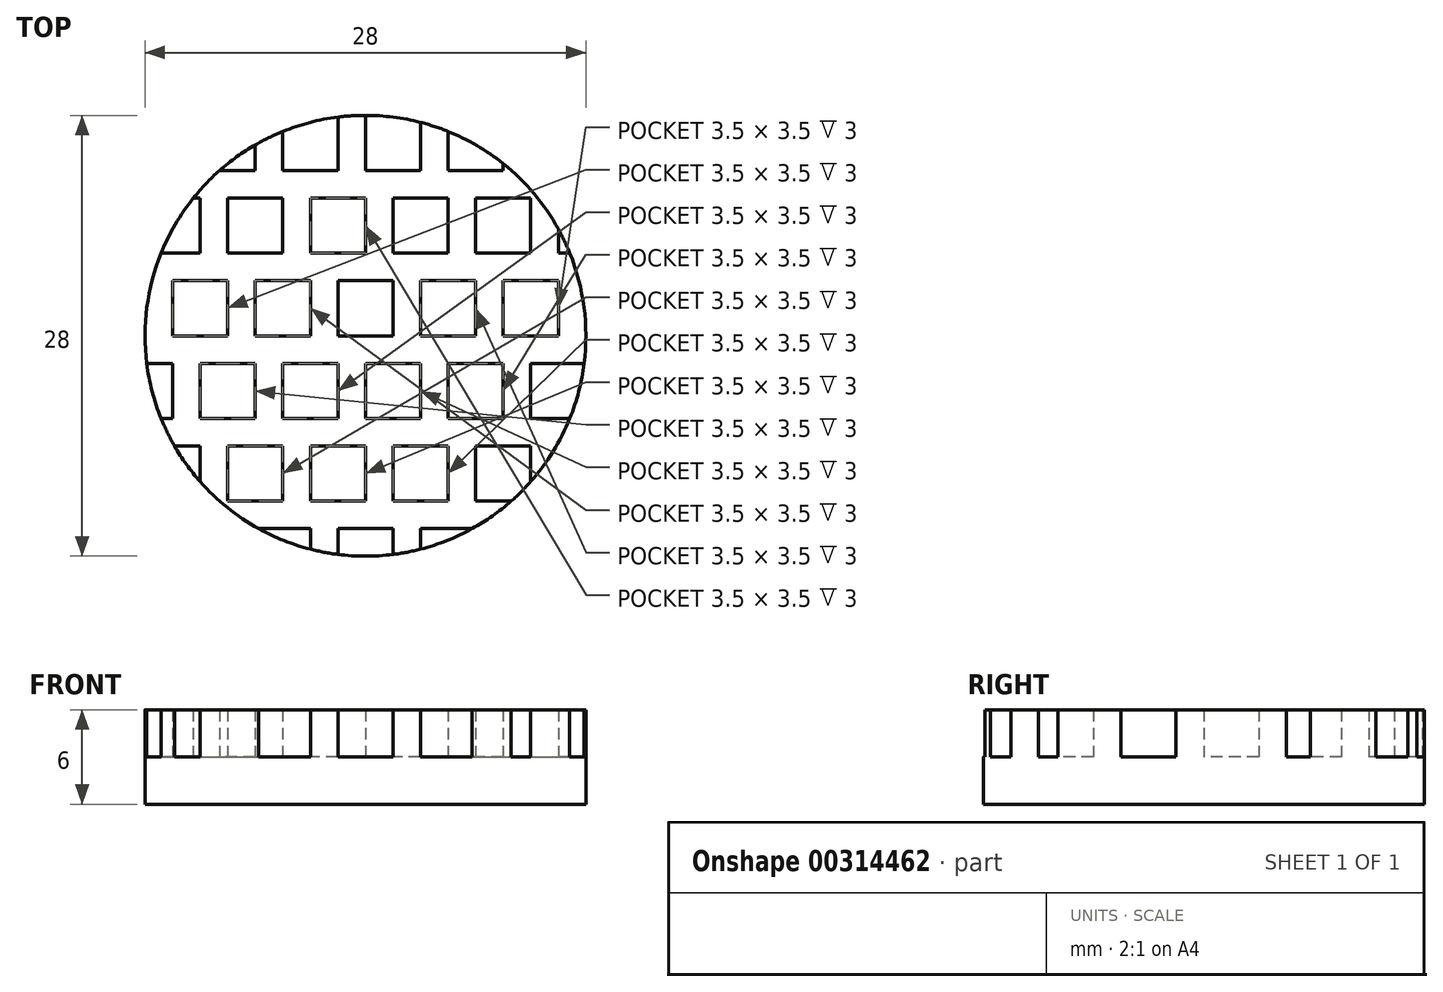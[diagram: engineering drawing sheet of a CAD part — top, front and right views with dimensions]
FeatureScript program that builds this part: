
annotation { "Feature Type Name" : "Feature", "Feature Type Description" : "" }
export const myFeature = defineFeature(function(context is Context, id is Id, definition is map)
    precondition{}
    {
        {
            var Q0;
            Q0=qCreatedBy(makeId("Top.planeOp"),FACE);
            var sketch = newSketch(context, id + "F0", { "sketchPlane" : qUnion([Q0])});
            skCircle(sketch, "E0", {"center": v(0, 0) * mm, "radius": 14 * mm});
            skSolve(sketch);
        }
        {
            var Q0;
            Q0=makeQuery(id+"F0.imprint","IMPRINT",FACE,{"disambiguationData":[TD([[makeQuery(id+"F0.imprint","IMPRINT",EDGE,{"derivedFrom":sQuery(id+"F0.wireOp",EDGE,"E0")}),1.0]])]});
            extrude(context, id + "F1", {"entities" : qUnion([Q0]), "depth" : 3 * mm});
        }
        {
            var Q0;
            Q0=makeQuery(id+"F1.opExtrude","CAP_FACE",FACE,{"disambiguationData":[OSD([sQuery(id+"F0.wireOp",EDGE,"E0")])],"isStart":false});
            var sketch = newSketch(context, id + "F2", { "sketchPlane" : qUnion([Q0])});
            skLineSegment(sketch, "E1.bottom", {"start": v(-10.5, 14) * mm, "end": v(-7, 14) * mm});
            skLineSegment(sketch, "E1.top", {"start": v(-10.5, 10.5) * mm, "end": v(-7, 10.5) * mm});
            skLineSegment(sketch, "E1.left", {"start": v(-10.5, 14) * mm, "end": v(-10.5, 10.5) * mm});
            skLineSegment(sketch, "E1.right", {"start": v(-7, 14) * mm, "end": v(-7, 10.5) * mm});
            skLineSegment(sketch, "E2.1.0.0", {"start": v(-5.25, 10.5) * mm, "end": v(-1.75, 10.5) * mm});
            skLineSegment(sketch, "E2.1.0.1", {"start": v(-5.25, 14) * mm, "end": v(-5.25, 10.5) * mm});
            skLineSegment(sketch, "E2.1.0.2", {"start": v(-1.75, 14) * mm, "end": v(-1.75, 10.5) * mm});
            skLineSegment(sketch, "E2.1.0.3", {"start": v(-5.25, 14) * mm, "end": v(-1.75, 14) * mm});
            skLineSegment(sketch, "E2.2.0.0", {"start": v(0, 10.5) * mm, "end": v(3.5, 10.5) * mm});
            skLineSegment(sketch, "E2.2.0.1", {"start": v(0, 14) * mm, "end": v(0, 10.5) * mm});
            skLineSegment(sketch, "E2.2.0.2", {"start": v(3.5, 14) * mm, "end": v(3.5, 10.5) * mm});
            skLineSegment(sketch, "E2.2.0.3", {"start": v(0, 14) * mm, "end": v(3.5, 14) * mm});
            skLineSegment(sketch, "E2.direction1", {"start": v(-10.5, 10.5) * mm, "end": v(-5.25, 10.5) * mm, "construction": true});
            skLineSegment(sketch, "E3.0.3.0", {"start": v(5.25, 10.5) * mm, "end": v(8.75, 10.5) * mm});
            skLineSegment(sketch, "E3.3.3.0", {"start": v(5.25, 14) * mm, "end": v(5.25, 10.5) * mm});
            skLineSegment(sketch, "E3.6.3.0", {"start": v(8.75, 14) * mm, "end": v(8.75, 10.5) * mm});
            skLineSegment(sketch, "E3.9.3.0", {"start": v(5.25, 14) * mm, "end": v(8.75, 14) * mm});
            skLineSegment(sketch, "E4.0.4.0", {"start": v(10.5, 10.5) * mm, "end": v(14, 10.5) * mm});
            skLineSegment(sketch, "E4.3.4.0", {"start": v(10.5, 14) * mm, "end": v(10.5, 10.5) * mm});
            skLineSegment(sketch, "E4.6.4.0", {"start": v(14, 14) * mm, "end": v(14, 10.5) * mm});
            skLineSegment(sketch, "E4.9.4.0", {"start": v(10.5, 14) * mm, "end": v(14, 14) * mm});
            skLineSegment(sketch, "E5.0.5.0", {"start": v(15.75, 10.5) * mm, "end": v(19.25, 10.5) * mm});
            skLineSegment(sketch, "E5.3.5.0", {"start": v(15.75, 14) * mm, "end": v(15.75, 10.5) * mm});
            skLineSegment(sketch, "E5.6.5.0", {"start": v(19.25, 14) * mm, "end": v(19.25, 10.5) * mm});
            skLineSegment(sketch, "E5.9.5.0", {"start": v(15.75, 14) * mm, "end": v(19.25, 14) * mm});
            skLineSegment(sketch, "E6.0.6.0", {"start": v(21, 10.5) * mm, "end": v(24.5, 10.5) * mm});
            skLineSegment(sketch, "E6.3.6.0", {"start": v(21, 14) * mm, "end": v(21, 10.5) * mm});
            skLineSegment(sketch, "E6.6.6.0", {"start": v(24.5, 14) * mm, "end": v(24.5, 10.5) * mm});
            skLineSegment(sketch, "E6.9.6.0", {"start": v(21, 14) * mm, "end": v(24.5, 14) * mm});
            skLineSegment(sketch, "E6.0.7.0", {"start": v(26.25, 10.5) * mm, "end": v(29.75, 10.5) * mm});
            skLineSegment(sketch, "E6.3.7.0", {"start": v(26.25, 14) * mm, "end": v(26.25, 10.5) * mm});
            skLineSegment(sketch, "E6.6.7.0", {"start": v(29.75, 14) * mm, "end": v(29.75, 10.5) * mm});
            skLineSegment(sketch, "E6.9.7.0", {"start": v(26.25, 14) * mm, "end": v(29.75, 14) * mm});
            skLineSegment(sketch, "E7.0.8.0", {"start": v(31.5, 10.5) * mm, "end": v(35, 10.5) * mm});
            skLineSegment(sketch, "E7.3.8.0", {"start": v(31.5, 14) * mm, "end": v(31.5, 10.5) * mm});
            skLineSegment(sketch, "E7.6.8.0", {"start": v(35, 14) * mm, "end": v(35, 10.5) * mm});
            skLineSegment(sketch, "E7.9.8.0", {"start": v(31.5, 14) * mm, "end": v(35, 14) * mm});
            skLineSegment(sketch, "E8.0.9.0", {"start": v(36.75, 10.5) * mm, "end": v(40.25, 10.5) * mm});
            skLineSegment(sketch, "E8.3.9.0", {"start": v(36.75, 14) * mm, "end": v(36.75, 10.5) * mm});
            skLineSegment(sketch, "E8.6.9.0", {"start": v(40.25, 14) * mm, "end": v(40.25, 10.5) * mm});
            skLineSegment(sketch, "E8.9.9.0", {"start": v(36.75, 14) * mm, "end": v(40.25, 14) * mm});
            skLineSegment(sketch, "E9.1.0.0", {"start": v(10.5, 8.75) * mm, "end": v(10.5, 5.25) * mm});
            skLineSegment(sketch, "E9.1.0.1", {"start": v(21, 8.75) * mm, "end": v(21, 5.25) * mm});
            skLineSegment(sketch, "E9.1.0.2", {"start": v(28, 8.75) * mm, "end": v(31.5, 8.75) * mm});
            skLineSegment(sketch, "E9.1.0.3", {"start": v(7, 8.75) * mm, "end": v(10.5, 8.75) * mm});
            skLineSegment(sketch, "E9.1.0.4", {"start": v(1.75, 8.75) * mm, "end": v(5.25, 8.75) * mm});
            skLineSegment(sketch, "E9.1.0.5", {"start": v(17.5, 8.75) * mm, "end": v(21, 8.75) * mm});
            skLineSegment(sketch, "E9.1.0.6", {"start": v(33.25, 8.75) * mm, "end": v(36.75, 8.75) * mm});
            skLineSegment(sketch, "E9.1.0.7", {"start": v(12.25, 8.75) * mm, "end": v(15.75, 8.75) * mm});
            skLineSegment(sketch, "E9.1.0.8", {"start": v(22.75, 8.75) * mm, "end": v(22.75, 5.25) * mm});
            skLineSegment(sketch, "E9.1.0.9", {"start": v(33.25, 5.25) * mm, "end": v(36.75, 5.25) * mm});
            skLineSegment(sketch, "E9.1.0.10", {"start": v(12.25, 5.25) * mm, "end": v(15.75, 5.25) * mm});
            skLineSegment(sketch, "E9.1.0.11", {"start": v(28, 5.25) * mm, "end": v(31.5, 5.25) * mm});
            skLineSegment(sketch, "E9.1.0.12", {"start": v(7, 5.25) * mm, "end": v(10.5, 5.25) * mm});
            skLineSegment(sketch, "E9.1.0.13", {"start": v(1.75, 5.25) * mm, "end": v(5.25, 5.25) * mm});
            skLineSegment(sketch, "E9.1.0.14", {"start": v(1.75, 8.75) * mm, "end": v(1.75, 5.25) * mm});
            skLineSegment(sketch, "E9.1.0.15", {"start": v(5.25, 8.75) * mm, "end": v(5.25, 5.25) * mm});
            skLineSegment(sketch, "E9.1.0.16", {"start": v(-14, 8.75) * mm, "end": v(-10.5, 8.75) * mm});
            skLineSegment(sketch, "E9.1.0.17", {"start": v(-10.5, 8.75) * mm, "end": v(-10.5, 5.25) * mm});
            skLineSegment(sketch, "E9.1.0.18", {"start": v(-8.75, 8.75) * mm, "end": v(-5.25, 8.75) * mm});
            skLineSegment(sketch, "E9.1.0.19", {"start": v(33.25, 8.75) * mm, "end": v(33.25, 5.25) * mm});
            skLineSegment(sketch, "E9.1.0.20", {"start": v(12.25, 8.75) * mm, "end": v(12.25, 5.25) * mm});
            skLineSegment(sketch, "E9.1.0.21", {"start": v(17.5, 5.25) * mm, "end": v(21, 5.25) * mm});
            skLineSegment(sketch, "E9.1.0.22", {"start": v(-14, 5.25) * mm, "end": v(-8.75, 5.25) * mm, "construction": true});
            skLineSegment(sketch, "E9.1.0.23", {"start": v(28, 8.75) * mm, "end": v(28, 5.25) * mm});
            skLineSegment(sketch, "E9.1.0.24", {"start": v(17.5, 8.75) * mm, "end": v(17.5, 5.25) * mm});
            skLineSegment(sketch, "E9.1.0.25", {"start": v(0, 8.75) * mm, "end": v(0, 5.25) * mm});
            skLineSegment(sketch, "E9.1.0.26", {"start": v(-3.5, 8.75) * mm, "end": v(0, 8.75) * mm});
            skLineSegment(sketch, "E9.1.0.27", {"start": v(7, 8.75) * mm, "end": v(7, 5.25) * mm});
            skLineSegment(sketch, "E9.1.0.28", {"start": v(31.5, 8.75) * mm, "end": v(31.5, 5.25) * mm});
            skLineSegment(sketch, "E9.1.0.29", {"start": v(-8.75, 5.25) * mm, "end": v(-5.25, 5.25) * mm});
            skLineSegment(sketch, "E9.1.0.30", {"start": v(-8.75, 8.75) * mm, "end": v(-8.75, 5.25) * mm});
            skLineSegment(sketch, "E9.1.0.31", {"start": v(-3.5, 5.25) * mm, "end": v(0, 5.25) * mm});
            skLineSegment(sketch, "E9.1.0.32", {"start": v(-3.5, 8.75) * mm, "end": v(-3.5, 5.25) * mm});
            skLineSegment(sketch, "E9.1.0.33", {"start": v(36.75, 8.75) * mm, "end": v(36.75, 5.25) * mm});
            skLineSegment(sketch, "E9.1.0.34", {"start": v(15.75, 8.75) * mm, "end": v(15.75, 5.25) * mm});
            skLineSegment(sketch, "E9.1.0.35", {"start": v(22.75, 5.25) * mm, "end": v(26.25, 5.25) * mm});
            skLineSegment(sketch, "E9.1.0.36", {"start": v(22.75, 8.75) * mm, "end": v(26.25, 8.75) * mm});
            skLineSegment(sketch, "E9.1.0.37", {"start": v(-14, 8.75) * mm, "end": v(-14, 5.25) * mm});
            skLineSegment(sketch, "E9.1.0.38", {"start": v(-5.25, 8.75) * mm, "end": v(-5.25, 5.25) * mm});
            skLineSegment(sketch, "E9.1.0.39", {"start": v(26.25, 8.75) * mm, "end": v(26.25, 5.25) * mm});
            skLineSegment(sketch, "E9.1.0.40", {"start": v(-14, 5.25) * mm, "end": v(-10.5, 5.25) * mm});
            skLineSegment(sketch, "E9.2.0.0", {"start": v(7, 3.5) * mm, "end": v(7, 0) * mm});
            skLineSegment(sketch, "E9.2.0.1", {"start": v(17.5, 3.5) * mm, "end": v(17.5, 0) * mm});
            skLineSegment(sketch, "E9.2.0.2", {"start": v(24.5, 3.5) * mm, "end": v(28, 3.5) * mm});
            skLineSegment(sketch, "E9.2.0.3", {"start": v(3.5, 3.5) * mm, "end": v(7, 3.5) * mm});
            skLineSegment(sketch, "E9.2.0.4", {"start": v(-1.75, 3.5) * mm, "end": v(1.75, 3.5) * mm});
            skLineSegment(sketch, "E9.2.0.5", {"start": v(14, 3.5) * mm, "end": v(17.5, 3.5) * mm});
            skLineSegment(sketch, "E9.2.0.6", {"start": v(29.75, 3.5) * mm, "end": v(33.25, 3.5) * mm});
            skLineSegment(sketch, "E9.2.0.7", {"start": v(8.75, 3.5) * mm, "end": v(12.25, 3.5) * mm});
            skLineSegment(sketch, "E9.2.0.8", {"start": v(19.25, 3.5) * mm, "end": v(19.25, 0) * mm});
            skLineSegment(sketch, "E9.2.0.9", {"start": v(29.75, 0) * mm, "end": v(33.25, 0) * mm});
            skLineSegment(sketch, "E9.2.0.10", {"start": v(8.75, 0) * mm, "end": v(12.25, 0) * mm});
            skLineSegment(sketch, "E9.2.0.11", {"start": v(24.5, 0) * mm, "end": v(28, 0) * mm});
            skLineSegment(sketch, "E9.2.0.12", {"start": v(3.5, 0) * mm, "end": v(7, 0) * mm});
            skLineSegment(sketch, "E9.2.0.13", {"start": v(-1.75, 0) * mm, "end": v(1.75, 0) * mm});
            skLineSegment(sketch, "E9.2.0.14", {"start": v(-1.75, 3.5) * mm, "end": v(-1.75, 0) * mm});
            skLineSegment(sketch, "E9.2.0.15", {"start": v(1.75, 3.5) * mm, "end": v(1.75, 0) * mm});
            skLineSegment(sketch, "E9.2.0.16", {"start": v(-17.5, 3.5) * mm, "end": v(-14, 3.5) * mm});
            skLineSegment(sketch, "E9.2.0.17", {"start": v(-14, 3.5) * mm, "end": v(-14, 0) * mm});
            skLineSegment(sketch, "E9.2.0.18", {"start": v(-12.25, 3.5) * mm, "end": v(-8.75, 3.5) * mm});
            skLineSegment(sketch, "E9.2.0.19", {"start": v(29.75, 3.5) * mm, "end": v(29.75, 0) * mm});
            skLineSegment(sketch, "E9.2.0.20", {"start": v(8.75, 3.5) * mm, "end": v(8.75, 0) * mm});
            skLineSegment(sketch, "E9.2.0.21", {"start": v(14, 0) * mm, "end": v(17.5, 0) * mm});
            skLineSegment(sketch, "E9.2.0.22", {"start": v(-17.5, 0) * mm, "end": v(-12.25, 0) * mm, "construction": true});
            skLineSegment(sketch, "E9.2.0.23", {"start": v(24.5, 3.5) * mm, "end": v(24.5, 0) * mm});
            skLineSegment(sketch, "E9.2.0.24", {"start": v(14, 3.5) * mm, "end": v(14, 0) * mm});
            skLineSegment(sketch, "E9.2.0.25", {"start": v(-3.5, 3.5) * mm, "end": v(-3.5, 0) * mm});
            skLineSegment(sketch, "E9.2.0.26", {"start": v(-7, 3.5) * mm, "end": v(-3.5, 3.5) * mm});
            skLineSegment(sketch, "E9.2.0.27", {"start": v(3.5, 3.5) * mm, "end": v(3.5, 0) * mm});
            skLineSegment(sketch, "E9.2.0.28", {"start": v(28, 3.5) * mm, "end": v(28, 0) * mm});
            skLineSegment(sketch, "E9.2.0.29", {"start": v(-12.25, 0) * mm, "end": v(-8.75, 0) * mm});
            skLineSegment(sketch, "E9.2.0.30", {"start": v(-12.25, 3.5) * mm, "end": v(-12.25, 0) * mm});
            skLineSegment(sketch, "E9.2.0.31", {"start": v(-7, 0) * mm, "end": v(-3.5, 0) * mm});
            skLineSegment(sketch, "E9.2.0.32", {"start": v(-7, 3.5) * mm, "end": v(-7, 0) * mm});
            skLineSegment(sketch, "E9.2.0.33", {"start": v(33.25, 3.5) * mm, "end": v(33.25, 0) * mm});
            skLineSegment(sketch, "E9.2.0.34", {"start": v(12.25, 3.5) * mm, "end": v(12.25, 0) * mm});
            skLineSegment(sketch, "E9.2.0.35", {"start": v(19.25, 0) * mm, "end": v(22.75, 0) * mm});
            skLineSegment(sketch, "E9.2.0.36", {"start": v(19.25, 3.5) * mm, "end": v(22.75, 3.5) * mm});
            skLineSegment(sketch, "E9.2.0.37", {"start": v(-17.5, 3.5) * mm, "end": v(-17.5, 0) * mm});
            skLineSegment(sketch, "E9.2.0.38", {"start": v(-8.75, 3.5) * mm, "end": v(-8.75, 0) * mm});
            skLineSegment(sketch, "E9.2.0.39", {"start": v(22.75, 3.5) * mm, "end": v(22.75, 0) * mm});
            skLineSegment(sketch, "E9.2.0.40", {"start": v(-17.5, 0) * mm, "end": v(-14, 0) * mm});
            skLineSegment(sketch, "E9.direction1", {"start": v(-10.5, 10.5) * mm, "end": v(-14, 5.25) * mm, "construction": true});
            skLineSegment(sketch, "E10.0.3.0", {"start": v(3.5, -1.75) * mm, "end": v(3.5, -5.25) * mm});
            skLineSegment(sketch, "E10.3.3.0", {"start": v(14, -1.75) * mm, "end": v(14, -5.25) * mm});
            skLineSegment(sketch, "E10.6.3.0", {"start": v(21, -1.75) * mm, "end": v(24.5, -1.75) * mm});
            skLineSegment(sketch, "E10.9.3.0", {"start": v(0, -1.75) * mm, "end": v(3.5, -1.75) * mm});
            skLineSegment(sketch, "E10.12.3.0", {"start": v(-5.25, -1.75) * mm, "end": v(-1.75, -1.75) * mm});
            skLineSegment(sketch, "E10.15.3.0", {"start": v(10.5, -1.75) * mm, "end": v(14, -1.75) * mm});
            skLineSegment(sketch, "E10.18.3.0", {"start": v(26.25, -1.75) * mm, "end": v(29.75, -1.75) * mm});
            skLineSegment(sketch, "E10.21.3.0", {"start": v(5.25, -1.75) * mm, "end": v(8.75, -1.75) * mm});
            skLineSegment(sketch, "E10.24.3.0", {"start": v(15.75, -1.75) * mm, "end": v(15.75, -5.25) * mm});
            skLineSegment(sketch, "E10.27.3.0", {"start": v(26.25, -5.25) * mm, "end": v(29.75, -5.25) * mm});
            skLineSegment(sketch, "E10.30.3.0", {"start": v(5.25, -5.25) * mm, "end": v(8.75, -5.25) * mm});
            skLineSegment(sketch, "E10.33.3.0", {"start": v(21, -5.25) * mm, "end": v(24.5, -5.25) * mm});
            skLineSegment(sketch, "E10.36.3.0", {"start": v(0, -5.25) * mm, "end": v(3.5, -5.25) * mm});
            skLineSegment(sketch, "E10.39.3.0", {"start": v(-5.25, -5.25) * mm, "end": v(-1.75, -5.25) * mm});
            skLineSegment(sketch, "E10.42.3.0", {"start": v(-5.25, -1.75) * mm, "end": v(-5.25, -5.25) * mm});
            skLineSegment(sketch, "E10.45.3.0", {"start": v(-1.75, -1.75) * mm, "end": v(-1.75, -5.25) * mm});
            skLineSegment(sketch, "E10.48.3.0", {"start": v(-21, -1.75) * mm, "end": v(-17.5, -1.75) * mm});
            skLineSegment(sketch, "E10.51.3.0", {"start": v(-17.5, -1.75) * mm, "end": v(-17.5, -5.25) * mm});
            skLineSegment(sketch, "E10.54.3.0", {"start": v(-15.75, -1.75) * mm, "end": v(-12.25, -1.75) * mm});
            skLineSegment(sketch, "E10.57.3.0", {"start": v(26.25, -1.75) * mm, "end": v(26.25, -5.25) * mm});
            skLineSegment(sketch, "E10.60.3.0", {"start": v(5.25, -1.75) * mm, "end": v(5.25, -5.25) * mm});
            skLineSegment(sketch, "E10.63.3.0", {"start": v(10.5, -5.25) * mm, "end": v(14, -5.25) * mm});
            skLineSegment(sketch, "E10.66.3.0", {"start": v(-21, -5.25) * mm, "end": v(-15.75, -5.25) * mm, "construction": true});
            skLineSegment(sketch, "E10.69.3.0", {"start": v(21, -1.75) * mm, "end": v(21, -5.25) * mm});
            skLineSegment(sketch, "E10.72.3.0", {"start": v(10.5, -1.75) * mm, "end": v(10.5, -5.25) * mm});
            skLineSegment(sketch, "E10.75.3.0", {"start": v(-7, -1.75) * mm, "end": v(-7, -5.25) * mm});
            skLineSegment(sketch, "E10.78.3.0", {"start": v(-10.5, -1.75) * mm, "end": v(-7, -1.75) * mm});
            skLineSegment(sketch, "E10.81.3.0", {"start": v(0, -1.75) * mm, "end": v(0, -5.25) * mm});
            skLineSegment(sketch, "E10.84.3.0", {"start": v(24.5, -1.75) * mm, "end": v(24.5, -5.25) * mm});
            skLineSegment(sketch, "E10.87.3.0", {"start": v(-15.75, -5.25) * mm, "end": v(-12.25, -5.25) * mm});
            skLineSegment(sketch, "E10.90.3.0", {"start": v(-15.75, -1.75) * mm, "end": v(-15.75, -5.25) * mm});
            skLineSegment(sketch, "E10.93.3.0", {"start": v(-10.5, -5.25) * mm, "end": v(-7, -5.25) * mm});
            skLineSegment(sketch, "E10.96.3.0", {"start": v(-10.5, -1.75) * mm, "end": v(-10.5, -5.25) * mm});
            skLineSegment(sketch, "E10.99.3.0", {"start": v(29.75, -1.75) * mm, "end": v(29.75, -5.25) * mm});
            skLineSegment(sketch, "E10.102.3.0", {"start": v(8.75, -1.75) * mm, "end": v(8.75, -5.25) * mm});
            skLineSegment(sketch, "E10.105.3.0", {"start": v(15.75, -5.25) * mm, "end": v(19.25, -5.25) * mm});
            skLineSegment(sketch, "E10.108.3.0", {"start": v(15.75, -1.75) * mm, "end": v(19.25, -1.75) * mm});
            skLineSegment(sketch, "E10.111.3.0", {"start": v(-21, -1.75) * mm, "end": v(-21, -5.25) * mm});
            skLineSegment(sketch, "E10.114.3.0", {"start": v(-12.25, -1.75) * mm, "end": v(-12.25, -5.25) * mm});
            skLineSegment(sketch, "E10.117.3.0", {"start": v(19.25, -1.75) * mm, "end": v(19.25, -5.25) * mm});
            skLineSegment(sketch, "E10.120.3.0", {"start": v(-21, -5.25) * mm, "end": v(-17.5, -5.25) * mm});
            skLineSegment(sketch, "E11.0.4.0", {"start": v(0, -7) * mm, "end": v(0, -10.5) * mm});
            skLineSegment(sketch, "E11.3.4.0", {"start": v(10.5, -7) * mm, "end": v(10.5, -10.5) * mm});
            skLineSegment(sketch, "E11.6.4.0", {"start": v(17.5, -7) * mm, "end": v(21, -7) * mm});
            skLineSegment(sketch, "E11.9.4.0", {"start": v(-3.5, -7) * mm, "end": v(0, -7) * mm});
            skLineSegment(sketch, "E11.12.4.0", {"start": v(-8.75, -7) * mm, "end": v(-5.25, -7) * mm});
            skLineSegment(sketch, "E11.15.4.0", {"start": v(7, -7) * mm, "end": v(10.5, -7) * mm});
            skLineSegment(sketch, "E11.18.4.0", {"start": v(22.75, -7) * mm, "end": v(26.25, -7) * mm});
            skLineSegment(sketch, "E11.21.4.0", {"start": v(1.75, -7) * mm, "end": v(5.25, -7) * mm});
            skLineSegment(sketch, "E11.24.4.0", {"start": v(12.25, -7) * mm, "end": v(12.25, -10.5) * mm});
            skLineSegment(sketch, "E11.27.4.0", {"start": v(22.75, -10.5) * mm, "end": v(26.25, -10.5) * mm});
            skLineSegment(sketch, "E11.30.4.0", {"start": v(1.75, -10.5) * mm, "end": v(5.25, -10.5) * mm});
            skLineSegment(sketch, "E11.33.4.0", {"start": v(17.5, -10.5) * mm, "end": v(21, -10.5) * mm});
            skLineSegment(sketch, "E11.36.4.0", {"start": v(-3.5, -10.5) * mm, "end": v(0, -10.5) * mm});
            skLineSegment(sketch, "E11.39.4.0", {"start": v(-8.75, -10.5) * mm, "end": v(-5.25, -10.5) * mm});
            skLineSegment(sketch, "E11.42.4.0", {"start": v(-8.75, -7) * mm, "end": v(-8.75, -10.5) * mm});
            skLineSegment(sketch, "E11.45.4.0", {"start": v(-5.25, -7) * mm, "end": v(-5.25, -10.5) * mm});
            skLineSegment(sketch, "E11.48.4.0", {"start": v(-24.5, -7) * mm, "end": v(-21, -7) * mm});
            skLineSegment(sketch, "E11.51.4.0", {"start": v(-21, -7) * mm, "end": v(-21, -10.5) * mm});
            skLineSegment(sketch, "E11.54.4.0", {"start": v(-19.25, -7) * mm, "end": v(-15.75, -7) * mm});
            skLineSegment(sketch, "E11.57.4.0", {"start": v(22.75, -7) * mm, "end": v(22.75, -10.5) * mm});
            skLineSegment(sketch, "E11.60.4.0", {"start": v(1.75, -7) * mm, "end": v(1.75, -10.5) * mm});
            skLineSegment(sketch, "E11.63.4.0", {"start": v(7, -10.5) * mm, "end": v(10.5, -10.5) * mm});
            skLineSegment(sketch, "E11.66.4.0", {"start": v(-24.5, -10.5) * mm, "end": v(-19.25, -10.5) * mm, "construction": true});
            skLineSegment(sketch, "E11.69.4.0", {"start": v(17.5, -7) * mm, "end": v(17.5, -10.5) * mm});
            skLineSegment(sketch, "E11.72.4.0", {"start": v(7, -7) * mm, "end": v(7, -10.5) * mm});
            skLineSegment(sketch, "E11.75.4.0", {"start": v(-10.5, -7) * mm, "end": v(-10.5, -10.5) * mm});
            skLineSegment(sketch, "E11.78.4.0", {"start": v(-14, -7) * mm, "end": v(-10.5, -7) * mm});
            skLineSegment(sketch, "E11.81.4.0", {"start": v(-3.5, -7) * mm, "end": v(-3.5, -10.5) * mm});
            skLineSegment(sketch, "E11.84.4.0", {"start": v(21, -7) * mm, "end": v(21, -10.5) * mm});
            skLineSegment(sketch, "E11.87.4.0", {"start": v(-19.25, -10.5) * mm, "end": v(-15.75, -10.5) * mm});
            skLineSegment(sketch, "E11.90.4.0", {"start": v(-19.25, -7) * mm, "end": v(-19.25, -10.5) * mm});
            skLineSegment(sketch, "E11.93.4.0", {"start": v(-14, -10.5) * mm, "end": v(-10.5, -10.5) * mm});
            skLineSegment(sketch, "E11.96.4.0", {"start": v(-14, -7) * mm, "end": v(-14, -10.5) * mm});
            skLineSegment(sketch, "E11.99.4.0", {"start": v(26.25, -7) * mm, "end": v(26.25, -10.5) * mm});
            skLineSegment(sketch, "E11.102.4.0", {"start": v(5.25, -7) * mm, "end": v(5.25, -10.5) * mm});
            skLineSegment(sketch, "E11.105.4.0", {"start": v(12.25, -10.5) * mm, "end": v(15.75, -10.5) * mm});
            skLineSegment(sketch, "E11.108.4.0", {"start": v(12.25, -7) * mm, "end": v(15.75, -7) * mm});
            skLineSegment(sketch, "E11.111.4.0", {"start": v(-24.5, -7) * mm, "end": v(-24.5, -10.5) * mm});
            skLineSegment(sketch, "E11.114.4.0", {"start": v(-15.75, -7) * mm, "end": v(-15.75, -10.5) * mm});
            skLineSegment(sketch, "E11.117.4.0", {"start": v(15.75, -7) * mm, "end": v(15.75, -10.5) * mm});
            skLineSegment(sketch, "E11.120.4.0", {"start": v(-24.5, -10.5) * mm, "end": v(-21, -10.5) * mm});
            skLineSegment(sketch, "E11.0.5.0", {"start": v(-3.5, -12.25) * mm, "end": v(-3.5, -15.75) * mm});
            skLineSegment(sketch, "E11.3.5.0", {"start": v(7, -12.25) * mm, "end": v(7, -15.75) * mm});
            skLineSegment(sketch, "E11.6.5.0", {"start": v(14, -12.25) * mm, "end": v(17.5, -12.25) * mm});
            skLineSegment(sketch, "E11.9.5.0", {"start": v(-7, -12.25) * mm, "end": v(-3.5, -12.25) * mm});
            skLineSegment(sketch, "E11.12.5.0", {"start": v(-12.25, -12.25) * mm, "end": v(-8.75, -12.25) * mm});
            skLineSegment(sketch, "E11.15.5.0", {"start": v(3.5, -12.25) * mm, "end": v(7, -12.25) * mm});
            skLineSegment(sketch, "E11.18.5.0", {"start": v(19.25, -12.25) * mm, "end": v(22.75, -12.25) * mm});
            skLineSegment(sketch, "E11.21.5.0", {"start": v(-1.75, -12.25) * mm, "end": v(1.75, -12.25) * mm});
            skLineSegment(sketch, "E11.24.5.0", {"start": v(8.75, -12.25) * mm, "end": v(8.75, -15.75) * mm});
            skLineSegment(sketch, "E11.27.5.0", {"start": v(19.25, -15.75) * mm, "end": v(22.75, -15.75) * mm});
            skLineSegment(sketch, "E11.30.5.0", {"start": v(-1.75, -15.75) * mm, "end": v(1.75, -15.75) * mm});
            skLineSegment(sketch, "E11.33.5.0", {"start": v(14, -15.75) * mm, "end": v(17.5, -15.75) * mm});
            skLineSegment(sketch, "E11.36.5.0", {"start": v(-7, -15.75) * mm, "end": v(-3.5, -15.75) * mm});
            skLineSegment(sketch, "E11.39.5.0", {"start": v(-12.25, -15.75) * mm, "end": v(-8.75, -15.75) * mm});
            skLineSegment(sketch, "E11.42.5.0", {"start": v(-12.25, -12.25) * mm, "end": v(-12.25, -15.75) * mm});
            skLineSegment(sketch, "E11.45.5.0", {"start": v(-8.75, -12.25) * mm, "end": v(-8.75, -15.75) * mm});
            skLineSegment(sketch, "E11.48.5.0", {"start": v(-28, -12.25) * mm, "end": v(-24.5, -12.25) * mm});
            skLineSegment(sketch, "E11.51.5.0", {"start": v(-24.5, -12.25) * mm, "end": v(-24.5, -15.75) * mm});
            skLineSegment(sketch, "E11.54.5.0", {"start": v(-22.75, -12.25) * mm, "end": v(-19.25, -12.25) * mm});
            skLineSegment(sketch, "E11.57.5.0", {"start": v(19.25, -12.25) * mm, "end": v(19.25, -15.75) * mm});
            skLineSegment(sketch, "E11.60.5.0", {"start": v(-1.75, -12.25) * mm, "end": v(-1.75, -15.75) * mm});
            skLineSegment(sketch, "E11.63.5.0", {"start": v(3.5, -15.75) * mm, "end": v(7, -15.75) * mm});
            skLineSegment(sketch, "E11.66.5.0", {"start": v(-28, -15.75) * mm, "end": v(-22.75, -15.75) * mm, "construction": true});
            skLineSegment(sketch, "E11.69.5.0", {"start": v(14, -12.25) * mm, "end": v(14, -15.75) * mm});
            skLineSegment(sketch, "E11.72.5.0", {"start": v(3.5, -12.25) * mm, "end": v(3.5, -15.75) * mm});
            skLineSegment(sketch, "E11.75.5.0", {"start": v(-14, -12.25) * mm, "end": v(-14, -15.75) * mm});
            skLineSegment(sketch, "E11.78.5.0", {"start": v(-17.5, -12.25) * mm, "end": v(-14, -12.25) * mm});
            skLineSegment(sketch, "E11.81.5.0", {"start": v(-7, -12.25) * mm, "end": v(-7, -15.75) * mm});
            skLineSegment(sketch, "E11.84.5.0", {"start": v(17.5, -12.25) * mm, "end": v(17.5, -15.75) * mm});
            skLineSegment(sketch, "E11.87.5.0", {"start": v(-22.75, -15.75) * mm, "end": v(-19.25, -15.75) * mm});
            skLineSegment(sketch, "E11.90.5.0", {"start": v(-22.75, -12.25) * mm, "end": v(-22.75, -15.75) * mm});
            skLineSegment(sketch, "E11.93.5.0", {"start": v(-17.5, -15.75) * mm, "end": v(-14, -15.75) * mm});
            skLineSegment(sketch, "E11.96.5.0", {"start": v(-17.5, -12.25) * mm, "end": v(-17.5, -15.75) * mm});
            skLineSegment(sketch, "E11.99.5.0", {"start": v(22.75, -12.25) * mm, "end": v(22.75, -15.75) * mm});
            skLineSegment(sketch, "E11.102.5.0", {"start": v(1.75, -12.25) * mm, "end": v(1.75, -15.75) * mm});
            skLineSegment(sketch, "E11.105.5.0", {"start": v(8.75, -15.75) * mm, "end": v(12.25, -15.75) * mm});
            skLineSegment(sketch, "E11.108.5.0", {"start": v(8.75, -12.25) * mm, "end": v(12.25, -12.25) * mm});
            skLineSegment(sketch, "E11.111.5.0", {"start": v(-28, -12.25) * mm, "end": v(-28, -15.75) * mm});
            skLineSegment(sketch, "E11.114.5.0", {"start": v(-19.25, -12.25) * mm, "end": v(-19.25, -15.75) * mm});
            skLineSegment(sketch, "E11.117.5.0", {"start": v(12.25, -12.25) * mm, "end": v(12.25, -15.75) * mm});
            skLineSegment(sketch, "E11.120.5.0", {"start": v(-28, -15.75) * mm, "end": v(-24.5, -15.75) * mm});
            skSolve(sketch);
        }
        {
            var Q0;
            {var subQ1=sQuery(id+"F2.wireOp",EDGE,"E2.1.0.0");Q0=makeQuery(id+"F2.imprint","IMPRINT",FACE,{"disambiguationData":[TD([[makeQuery(id+"F2.imprint","IMPRINT",EDGE,{"derivedFrom":subQ1}),-1.0]])]});}
            extrude(context, id + "F3", {"entities" : qUnion([Q0]), "operationType" : NewBodyOperationType.ADD, "depth" : 3 * mm});
        }
    });
